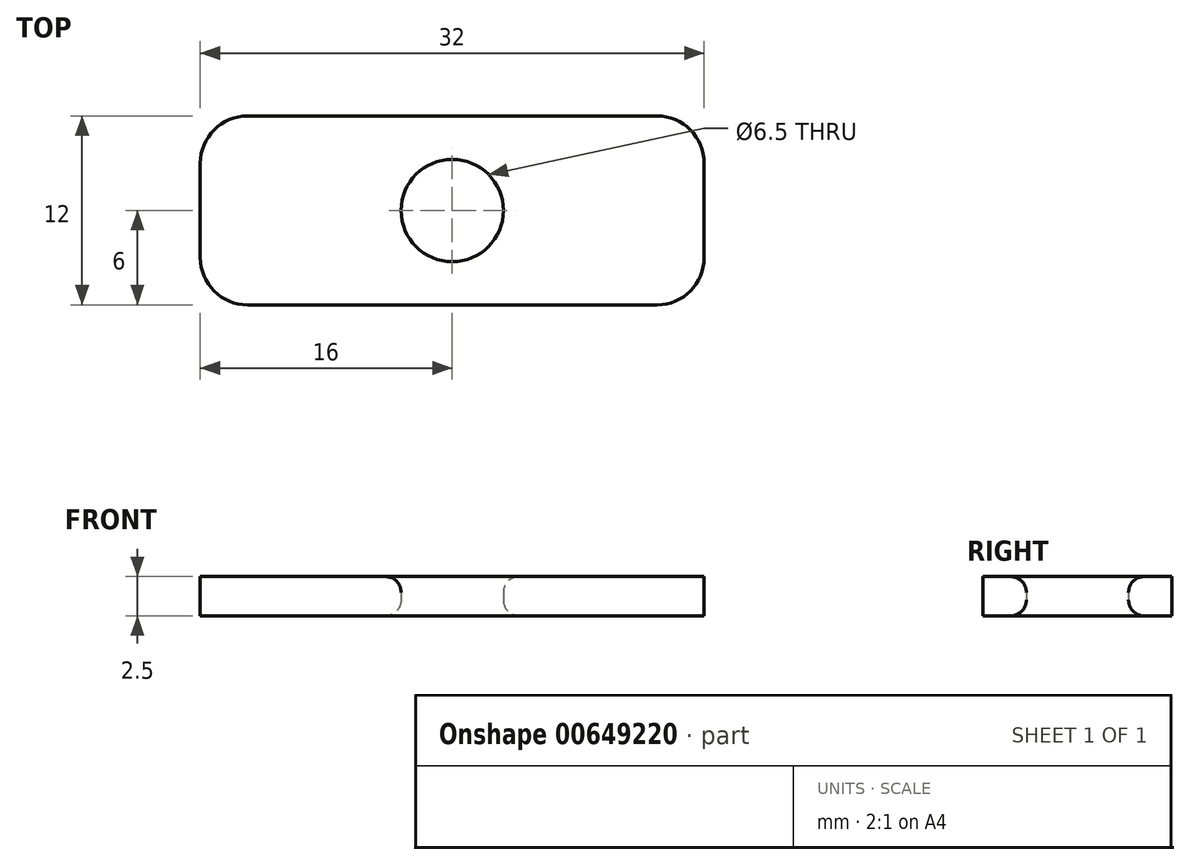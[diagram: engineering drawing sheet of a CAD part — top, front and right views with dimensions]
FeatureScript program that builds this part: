
annotation { "Feature Type Name" : "Feature", "Feature Type Description" : "" }
export const myFeature = defineFeature(function(context is Context, id is Id, definition is map)
    precondition{}
    {
        {
            var Q0;
            Q0=qCreatedBy(makeId("Top.planeOp"),FACE);
            var sketch = newSketch(context, id + "F0", { "sketchPlane" : qUnion([Q0])});
            skLineSegment(sketch, "E0", {"start": v(0, 0) * mm, "end": v(0, -37.37) * mm, "construction": true});
            skLineSegment(sketch, "E1", {"start": v(0, -37.37) * mm, "end": v(0, 38.39) * mm, "construction": true});
            skLineSegment(sketch, "E2", {"start": v(-34.71, 0) * mm, "end": v(35.12, 0) * mm, "construction": true});
            skLineSegment(sketch, "E3.0", {"start": v(16, -6) * mm, "end": v(16, 6) * mm, "construction": true});
            skLineSegment(sketch, "E4.0", {"start": v(-16, -6) * mm, "end": v(-16, 6) * mm});
            skLineSegment(sketch, "E5.0", {"start": v(-16, -6) * mm, "end": v(16, -6) * mm, "construction": true});
            skLineSegment(sketch, "E6.0", {"start": v(-16, 6) * mm, "end": v(16, 6) * mm});
            skLineSegment(sketch, "E7", {"start": v(-16, -6) * mm, "end": v(16, -6) * mm});
            skLineSegment(sketch, "E8", {"start": v(16, -6) * mm, "end": v(16, 6) * mm});
            skCircle(sketch, "E9", {"center": v(0, 0) * mm, "radius": 3.25 * mm});
            skSolve(sketch);
        }
        {
            var Q0;
            Q0=makeQuery(id+"F0.imprint","IMPRINT",FACE,{"disambiguationData":[TD([[makeQuery(id+"F0.imprint","IMPRINT",EDGE,{"derivedFrom":sQuery(id+"F0.wireOp",EDGE,"E4.0")}),-1.0]])]});
            extrude(context, id + "F1", {"entities" : qUnion([Q0]), "depth" : 2.5 * mm, "offsetDistance" : 25 * mm});
        }
        {
            var Q0;
            Q0=makeQuery(id+"F1.opExtrude","SWEPT_EDGE",EDGE,{"disambiguationData":[OSD([sQuery(id+"F0.wireOp",EDGE,"E4.0"),sQuery(id+"F0.wireOp",EDGE,"E6.0")])]});
            var Q1;
            Q1=makeQuery(id+"F1.opExtrude","SWEPT_EDGE",EDGE,{"disambiguationData":[OSD([sQuery(id+"F0.wireOp",EDGE,"E4.0"),sQuery(id+"F0.wireOp",EDGE,"E7")])]});
            var Q2;
            Q2=makeQuery(id+"F1.opExtrude","SWEPT_EDGE",EDGE,{"disambiguationData":[OSD([sQuery(id+"F0.wireOp",EDGE,"E6.0"),sQuery(id+"F0.wireOp",EDGE,"E8")])]});
            var Q3;
            Q3=makeQuery(id+"F1.opExtrude","SWEPT_EDGE",EDGE,{"disambiguationData":[OSD([sQuery(id+"F0.wireOp",EDGE,"E7"),sQuery(id+"F0.wireOp",EDGE,"E8")])]});
            fillet(context, id + "F2", {"entities" : qUnion([Q0, Q1, Q2, Q3]), "radius" : 3 * mm, "tangentPropagation" : true, "allowEdgeOverflow" : false});
        }
        {
            var Q0;
            Q0=makeQuery(id+"F1.opExtrude","CAP_EDGE",EDGE,{"disambiguationData":[OSD([sQuery(id+"F0.wireOp",EDGE,"E9")])],"isStart":false});
            var Q1;
            Q1=makeQuery(id+"F1.opExtrude","CAP_EDGE",EDGE,{"disambiguationData":[OSD([sQuery(id+"F0.wireOp",EDGE,"E9")])],"isStart":true});
            fillet(context, id + "F3", {"entities" : qUnion([Q0, Q1]), "radius" : 1 * mm, "tangentPropagation" : true, "allowEdgeOverflow" : false});
        }
    });
